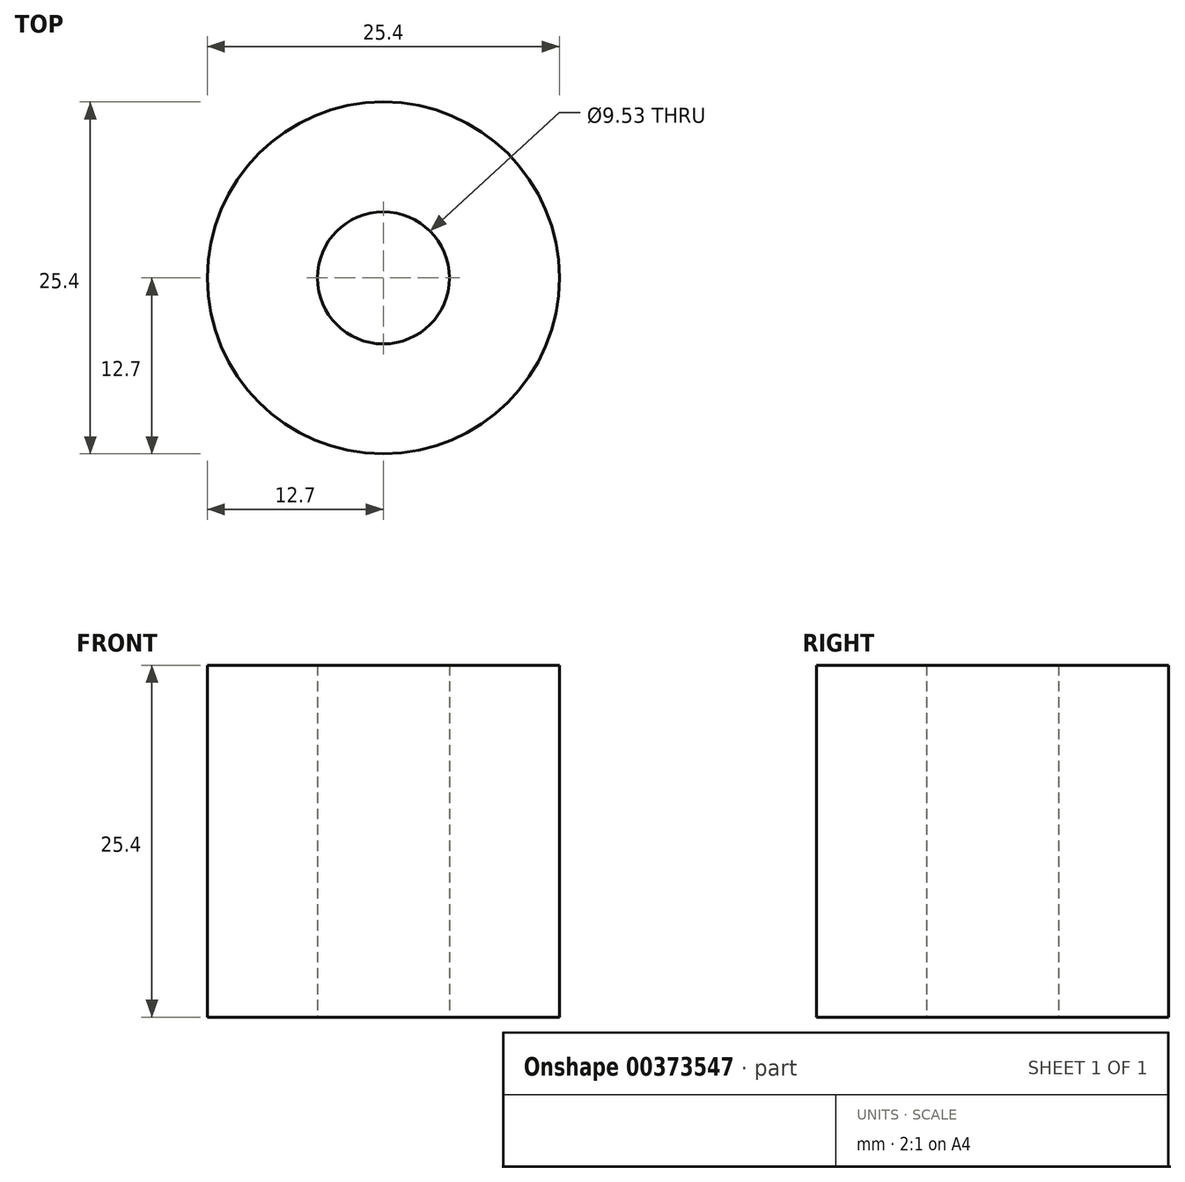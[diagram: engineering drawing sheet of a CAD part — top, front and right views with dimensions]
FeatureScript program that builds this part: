
annotation { "Feature Type Name" : "Feature", "Feature Type Description" : "" }
export const myFeature = defineFeature(function(context is Context, id is Id, definition is map)
    precondition{}
    {
        {
            var Q0;
            Q0=qCreatedBy(makeId("Top.planeOp"),FACE);
            var sketch = newSketch(context, id + "F0", { "sketchPlane" : qUnion([Q0])});
            skCircle(sketch, "E0", {"center": v(0, 0) * mm, "radius": 12.7 * mm});
            skCircle(sketch, "E1", {"center": v(0, 0) * mm, "radius": 6.35 * mm});
            skCircle(sketch, "E2", {"center": v(0, 0) * mm, "radius": 4.76 * mm});
            skSolve(sketch);
        }
        {
            var Q0;
            Q0=makeQuery(id+"F0.imprint","IMPRINT",FACE,{"disambiguationData":[TD([[makeQuery(id+"F0.imprint","IMPRINT",EDGE,{"derivedFrom":sQuery(id+"F0.wireOp",EDGE,"E1")}),1.0]])]});
            var Q1;
            Q1=makeQuery(id+"F0.imprint","IMPRINT",FACE,{"disambiguationData":[TD([[makeQuery(id+"F0.imprint","IMPRINT",EDGE,{"derivedFrom":sQuery(id+"F0.wireOp",EDGE,"E0")}),1.0]])]});
            extrude(context, id + "F1", {"entities" : qUnion([Q0, Q1]), "depth" : 25.4 * mm});
        }
    });
